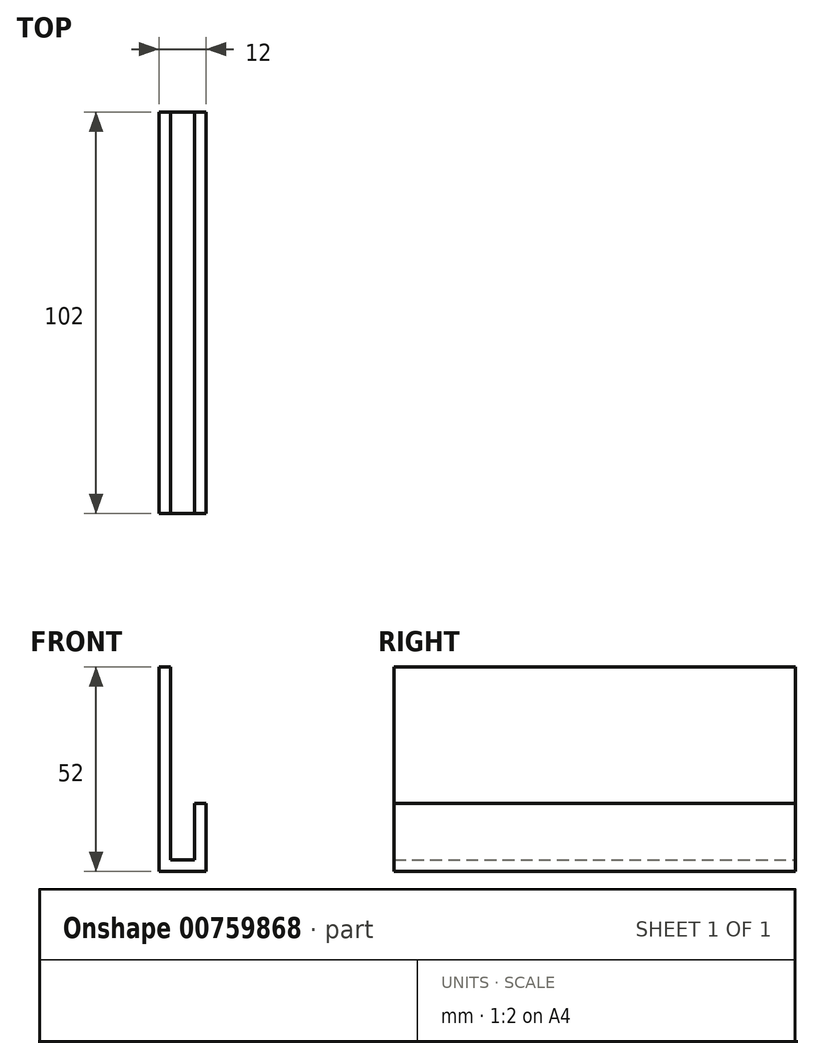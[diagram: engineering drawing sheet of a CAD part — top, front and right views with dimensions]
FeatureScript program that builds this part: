
annotation { "Feature Type Name" : "Feature", "Feature Type Description" : "" }
export const myFeature = defineFeature(function(context is Context, id is Id, definition is map)
    precondition{}
    {
        {
            var Q0;
            Q0=qCreatedBy(makeId("Front.planeOp"),FACE);
            var sketch = newSketch(context, id + "F0", { "sketchPlane" : qUnion([Q0])});
            skLineSegment(sketch, "E0", {"start": v(0, 26) * mm, "end": v(0, -26) * mm});
            skLineSegment(sketch, "E1", {"start": v(0, -26) * mm, "end": v(12, -26) * mm});
            skLineSegment(sketch, "E2", {"start": v(12, -26) * mm, "end": v(12, -8.67) * mm});
            skLineSegment(sketch, "E3", {"start": v(12, -8.67) * mm, "end": v(9, -8.67) * mm});
            skLineSegment(sketch, "E4", {"start": v(9, -8.67) * mm, "end": v(9, -23) * mm});
            skLineSegment(sketch, "E5", {"start": v(9, -23) * mm, "end": v(3, -23) * mm});
            skLineSegment(sketch, "E6", {"start": v(3, -23) * mm, "end": v(3, 26) * mm});
            skLineSegment(sketch, "E7", {"start": v(3, 26) * mm, "end": v(0, 26) * mm});
            skSolve(sketch);
        }
        {
            var Q0;
            Q0=makeQuery(id+"F0.imprint","IMPRINT",FACE,{"disambiguationData":[TD([[makeQuery(id+"F0.imprint","IMPRINT",EDGE,{"derivedFrom":sQuery(id+"F0.wireOp",EDGE,"E0")}),1.0]])]});
            extrude(context, id + "F1", {"entities" : qUnion([Q0]), "endBound" : BoundingType.SYMMETRIC, "depth" : 102 * mm, "offsetDistance" : 25 * mm});
        }
    });
